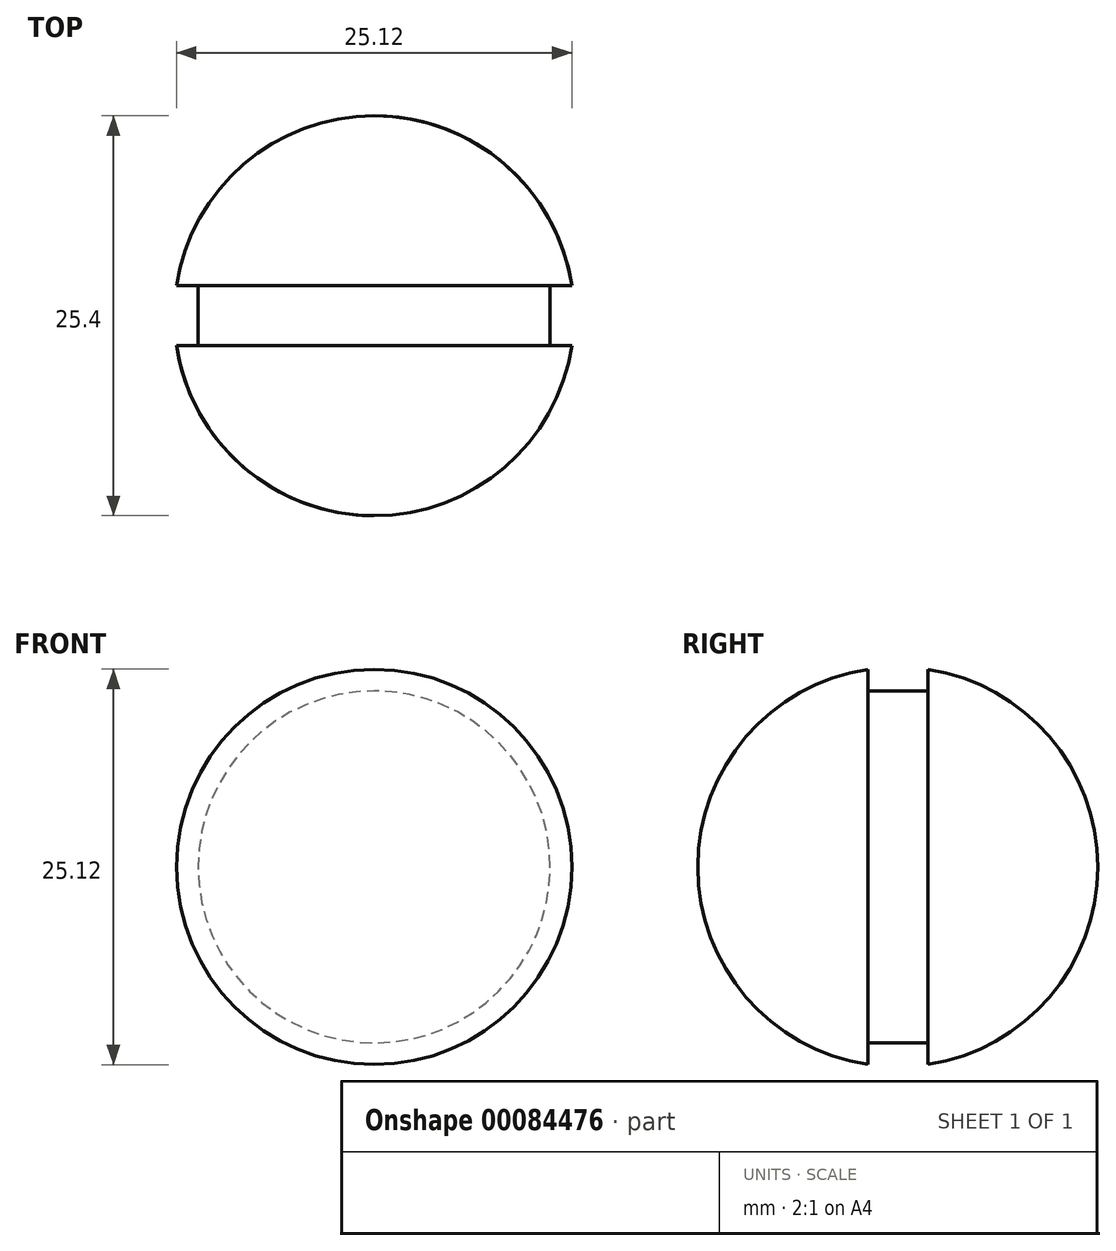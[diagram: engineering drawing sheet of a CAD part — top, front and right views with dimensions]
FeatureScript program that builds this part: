
annotation { "Feature Type Name" : "Feature", "Feature Type Description" : "" }
export const myFeature = defineFeature(function(context is Context, id is Id, definition is map)
    precondition{}
    {
        {
            var Q0;
            Q0=qCreatedBy(makeId("Top.planeOp"),FACE);
            var sketch = newSketch(context, id + "F0", { "sketchPlane" : qUnion([Q0])});
            skCircle(sketch, "E0", {"center": v(0, 0) * mm, "radius": 12.7 * mm});
            skLineSegment(sketch, "E1", {"start": v(0, -12.7) * mm, "end": v(0, 12.7) * mm});
            skLineSegment(sketch, "E2", {"start": v(0, 12.7) * mm, "end": v(0, -12.7) * mm});
            skPoint(sketch, "E3.middle", {"position": v(0, -12.7) * mm});
            skLineSegment(sketch, "E4.bottom", {"start": v(14.22, 1.9) * mm, "end": v(11.18, 1.9) * mm});
            skLineSegment(sketch, "E4.top", {"start": v(14.22, -1.9) * mm, "end": v(11.18, -1.9) * mm});
            skLineSegment(sketch, "E4.left", {"start": v(14.22, 1.9) * mm, "end": v(14.22, -1.9) * mm});
            skLineSegment(sketch, "E4.right", {"start": v(11.18, 1.9) * mm, "end": v(11.18, -1.9) * mm});
            skPoint(sketch, "E4.middle", {"position": v(12.7, 0) * mm});
            skSolve(sketch);
        }
        {
            var Q0;
            {var subQ7=sQuery(id+"F0.wireOp",EDGE,"E4.right");Q0=makeQuery(id+"F0.imprint","IMPRINT",FACE,{"disambiguationData":[TD([[makeQuery(id+"F0.imprint","IMPRINT",EDGE,{"derivedFrom":subQ7}),-1.0]])]});}
            var Q1;
            Q1=sQuery(id+"F0.wireOp",EDGE,"E1");
            revolve(context, id + "F1", {"entities" : qUnion([Q0]), "axis" : qUnion([Q1]), "revolveType" : RevolveType.FULL});
        }
    });
